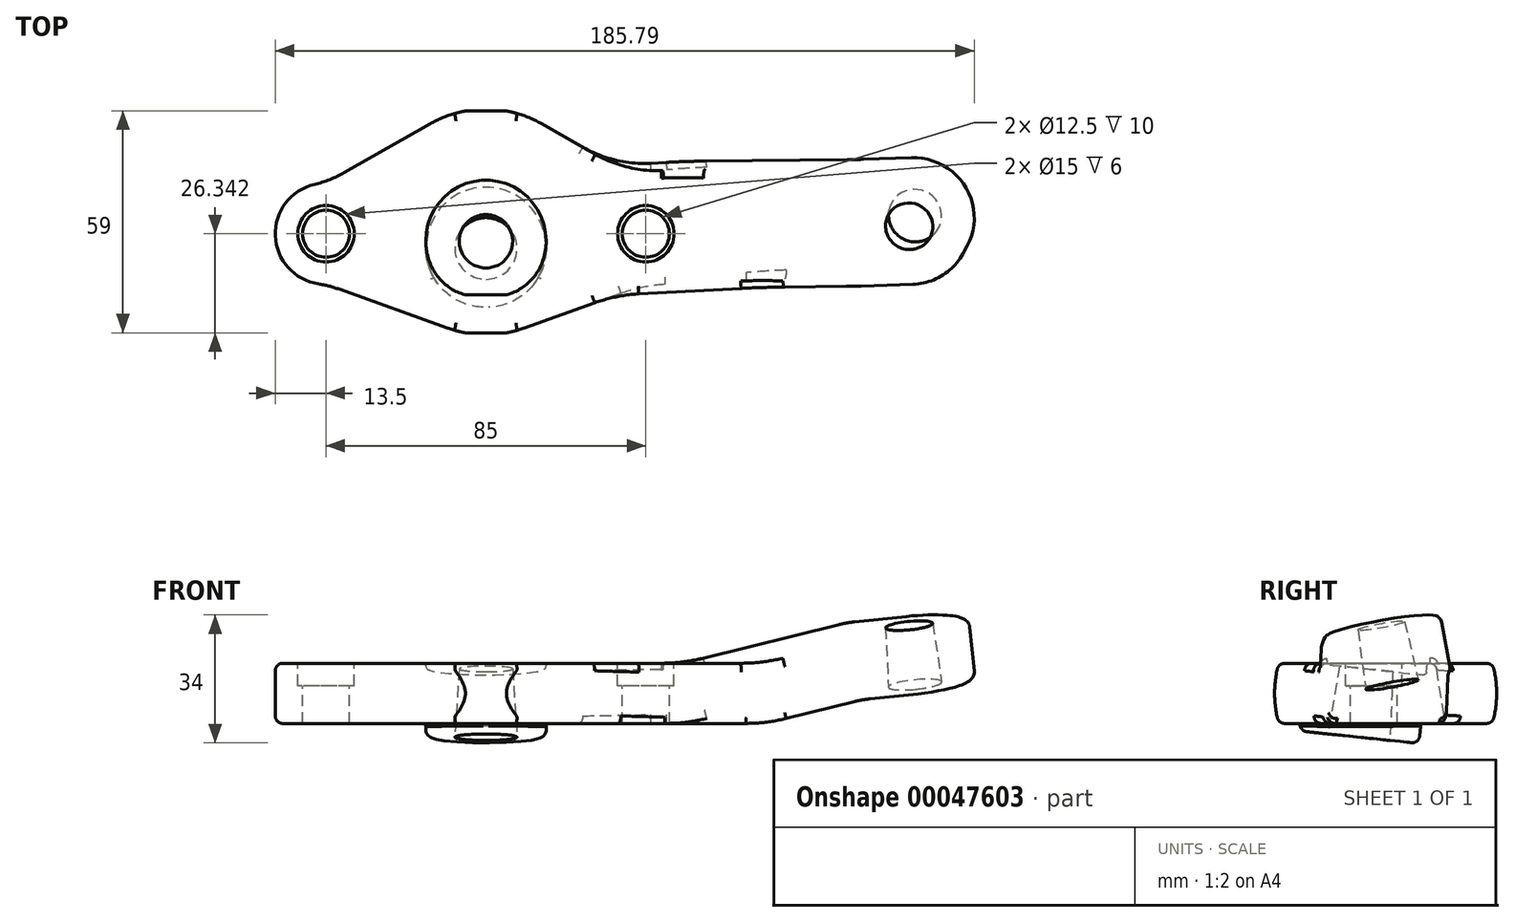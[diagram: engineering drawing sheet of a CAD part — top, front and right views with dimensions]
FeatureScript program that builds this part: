
annotation { "Feature Type Name" : "Feature", "Feature Type Description" : "" }
export const myFeature = defineFeature(function(context is Context, id is Id, definition is map)
    precondition{}
    {
        {
            var Q0;
            Q0=qCreatedBy(makeId("Top.planeOp"),FACE);
            var sketch = newSketch(context, id + "F0", { "sketchPlane" : qUnion([Q0])});
            skCircle(sketch, "E0", {"center": v(0, 0) * mm, "radius": 5 * mm});
            skCircle(sketch, "E1", {"center": v(0, 0) * mm, "radius": 15 * mm});
            skCircle(sketch, "E2", {"center": v(42.5, 1.84) * mm, "radius": 6.25 * mm});
            skCircle(sketch, "E3", {"center": v(42.5, 1.84) * mm, "radius": 7.5 * mm});
            skCircle(sketch, "E4", {"center": v(113.5, 5.65) * mm, "radius": 5 * mm});
            skArc(sketch, "E5", {"start": v(114.35, -10.32) * mm, "mid": v(129.47, 6.51) * mm, "end": v(112.63, 21.63) * mm});
            skCircle(sketch, "E6", {"center": v(-42.5, 1.84) * mm, "radius": 6.25 * mm});
            skCircle(sketch, "E7", {"center": v(-42.5, 1.84) * mm, "radius": 7.5 * mm});
            skLineSegment(sketch, "E8", {"start": v(-42.5, 25) * mm, "end": v(-42.5, -32.02) * mm, "construction": true});
            skArc(sketch, "E9", {"start": v(-44.55, -11.5) * mm, "mid": v(-55.99, 1.31) * mm, "end": v(-45.6, 14.98) * mm});
            skArc(sketch, "E10", {"start": v(-10.1, -23.25) * mm, "mid": v(0, -25) * mm, "end": v(10.1, -23.25) * mm});
            skLineSegment(sketch, "E11", {"start": v(-37.64, 18.1) * mm, "end": v(-14.83, 31.08) * mm});
            skLineSegment(sketch, "E12", {"start": v(-39.02, -12.9) * mm, "end": v(-10.1, -23.25) * mm});
            skLineSegment(sketch, "E13", {"start": v(42.5, 1.84) * mm, "end": v(113.5, 5.65) * mm, "construction": true});
            skLineSegment(sketch, "E14", {"start": v(112.63, 21.63) * mm, "end": v(47.23, 18.12) * mm});
            skLineSegment(sketch, "E15", {"start": v(114.35, -10.32) * mm, "end": v(38.57, -14.4) * mm});
            skLineSegment(sketch, "E16", {"start": v(42.5, -32.88) * mm, "end": v(42.5, 48.6) * mm, "construction": true});
            skArc(sketch, "E17", {"start": v(42.5, -11.66) * mm, "mid": v(56, 1.84) * mm, "end": v(42.5, 15.34) * mm, "construction": true});
            skLineSegment(sketch, "E18", {"start": v(30.8, 22) * mm, "end": v(14.83, 31.08) * mm});
            skLineSegment(sketch, "E19", {"start": v(30.08, -16.1) * mm, "end": v(10.1, -23.25) * mm});
            skArc(sketch, "E20.trimOffspring", {"start": v(14.83, 31.08) * mm, "mid": v(0, 35) * mm, "end": v(-14.83, 31.08) * mm});
            skArc(sketch, "E21.filletArc", {"start": v(30.8, 22) * mm, "mid": v(38.74, 18.88) * mm, "end": v(47.23, 18.12) * mm});
            skArc(sketch, "E22.filletArc", {"start": v(38.57, -14.4) * mm, "mid": v(34.26, -14.94) * mm, "end": v(30.08, -16.1) * mm});
            skPoint(sketch, "E23.visualSharp", {"position": v(-42.5, -11.66) * mm});
            skArc(sketch, "E23.filletArc", {"start": v(-39.02, -12.9) * mm, "mid": v(-41.75, -12.07) * mm, "end": v(-44.55, -11.5) * mm});
            skPoint(sketch, "E24.visualSharp", {"position": v(-42.5, 15.34) * mm});
            skArc(sketch, "E24.filletArc", {"start": v(-45.6, 14.98) * mm, "mid": v(-41.5, 16.26) * mm, "end": v(-37.64, 18.1) * mm});
            skLineSegment(sketch, "E25", {"start": v(96.66, 20.77) * mm, "end": v(98.37, -11.18) * mm});
            skSolve(sketch);
        }
        {
            var Q0;
            Q0=qCreatedBy(makeId("Top.planeOp"),FACE);
            cPlane(context, id + "F1", {"entities" : qUnion([Q0]), "cplaneType" : CPlaneType.OFFSET, "offset" : 10.43 * mm, "width" : 150 * mm, "height" : 150 * mm});
        }
        {
            var Q0;
            Q0=qCreatedBy(id+"F1.planeOp",FACE);
            var sketch = newSketch(context, id + "F2", { "sketchPlane" : qUnion([Q0])});
            skPoint(sketch, "E26.0", {"position": v(113.5, 5.65) * mm});
            skLineSegment(sketch, "E27", {"start": v(114.74, -17.54) * mm, "end": v(111.9, 35.31) * mm, "construction": true});
            skLineSegment(sketch, "E28.0", {"start": v(96.66, 20.77) * mm, "end": v(98.37, -11.18) * mm, "construction": true});
            skSolve(sketch);
        }
        {
            var Q0;
            Q0=sQuery(id+"F2.wireOp",EDGE,"E27");
            var Q1;
            Q1=qCreatedBy(id+"F1.planeOp",FACE);
            cPlane(context, id + "F3", {"entities" : qUnion([Q0, Q1]), "cplaneType" : CPlaneType.LINE_ANGLE, "offset" : 150 * mm, "angle" : 353.8 * degree, "width" : 150 * mm, "height" : 150 * mm});
        }
        {
            var Q0;
            Q0=qCreatedBy(id+"F3.planeOp",FACE);
            var sketch = newSketch(context, id + "F4", { "sketchPlane" : qUnion([Q0])});
            skLineSegment(sketch, "E29.0", {"start": v(42.25, -1.84) * mm, "end": v(112.83, -5.65) * mm});
            skSolve(sketch);
        }
        {
            var Q0;
            Q0=sQuery(id+"F4.wireOp",EDGE,"E29.0");
            var Q1;
            Q1=qCreatedBy(id+"F3.planeOp",FACE);
            cPlane(context, id + "F5", {"entities" : qUnion([Q0, Q1]), "cplaneType" : CPlaneType.LINE_ANGLE, "offset" : 150 * mm, "angle" : 9.9 * degree, "width" : 150 * mm, "height" : 150 * mm});
        }
        {
            var Q0;
            Q0=qCreatedBy(id+"F5.planeOp",FACE);
            var sketch = newSketch(context, id + "F6", { "sketchPlane" : qUnion([Q0])});
            skPoint(sketch, "E30.0", {"position": v(112.86, 5.56) * mm});
            skArc(sketch, "E31", {"start": v(113.7, -10.41) * mm, "mid": v(128.84, 6.41) * mm, "end": v(112, 21.54) * mm});
            skLineSegment(sketch, "E32.0", {"start": v(42.27, 1.81) * mm, "end": v(112.86, 5.56) * mm, "construction": true});
            skLineSegment(sketch, "E33", {"start": v(96.03, 20.7) * mm, "end": v(112, 21.54) * mm});
            skLineSegment(sketch, "E34", {"start": v(97.73, -11.26) * mm, "end": v(113.7, -10.41) * mm});
            skLineSegment(sketch, "E35", {"start": v(96.03, 20.7) * mm, "end": v(97.73, -11.26) * mm});
            skCircle(sketch, "E36", {"center": v(112.86, 5.56) * mm, "radius": 5 * mm});
            skSolve(sketch);
        }
        {
            var Q0;
            Q0=makeQuery(id+"F6.imprint","IMPRINT",FACE,{"disambiguationData":[TD([[makeQuery(id+"F6.imprint","IMPRINT",EDGE,{"derivedFrom":sQuery(id+"F6.wireOp",EDGE,"E31")}),1.0]])]});
            extrude(context, id + "F7", {"entities" : qUnion([Q0]), "oppositeDirection" : true, "depth" : 16 * mm});
        }
        {
            var Q0;
            Q0=sQuery(id+"F6.wireOp",EDGE,"E35");
            var Q1;
            Q1=qCreatedBy(id+"F5.planeOp",FACE);
            cPlane(context, id + "F8", {"entities" : qUnion([Q0, Q1]), "cplaneType" : CPlaneType.LINE_ANGLE, "offset" : 150 * mm, "angle" : 8 * degree, "width" : 150 * mm, "height" : 150 * mm});
        }
        {
            var Q0;
            Q0=qCreatedBy(id+"F8.planeOp",FACE);
            var sketch = newSketch(context, id + "F9", { "sketchPlane" : qUnion([Q0])});
            skLineSegment(sketch, "E37.0", {"start": v(94.81, -20.75) * mm, "end": v(96.55, 11.2) * mm});
            skLineSegment(sketch, "E38.0", {"start": v(41.6, -1.83) * mm, "end": v(111.5, -5.63) * mm, "construction": true});
            skLineSegment(sketch, "E39", {"start": v(94.81, -20.75) * mm, "end": v(24.92, -16.95) * mm});
            skLineSegment(sketch, "E40", {"start": v(96.55, 11.2) * mm, "end": v(26.65, 15) * mm});
            skLineSegment(sketch, "E41", {"start": v(24.92, -16.95) * mm, "end": v(26.65, 15) * mm});
            skSolve(sketch);
        }
        {
            var Q0;
            Q0 = qSketchRegion(id + "F9", true);
            extrude(context, id + "F10", {"entities" : qUnion([Q0]), "operationType" : NewBodyOperationType.ADD, "depth" : 16 * mm});
        }
        {
            var Q0;
            Q0=qCreatedBy(makeId("Top.planeOp"),FACE);
            var sketch = newSketch(context, id + "F11", { "sketchPlane" : qUnion([Q0])});
            skLineSegment(sketch, "E42.0", {"start": v(30.8, 22) * mm, "end": v(14.83, 31.08) * mm});
            skArc(sketch, "E43.0", {"start": v(14.83, 31.08) * mm, "mid": v(0, 35) * mm, "end": v(-14.83, 31.08) * mm});
            skLineSegment(sketch, "E44.0", {"start": v(-37.64, 18.1) * mm, "end": v(-14.83, 31.08) * mm});
            skArc(sketch, "E45.0", {"start": v(-45.6, 14.98) * mm, "mid": v(-41.5, 16.26) * mm, "end": v(-37.64, 18.1) * mm});
            skArc(sketch, "E46.0", {"start": v(-44.55, -11.5) * mm, "mid": v(-55.99, 1.31) * mm, "end": v(-45.6, 14.98) * mm});
            skArc(sketch, "E47.0", {"start": v(-39.02, -12.9) * mm, "mid": v(-41.75, -12.07) * mm, "end": v(-44.55, -11.5) * mm});
            skLineSegment(sketch, "E48.0", {"start": v(-39.02, -12.9) * mm, "end": v(-10.1, -23.25) * mm});
            skArc(sketch, "E49.0", {"start": v(-10.1, -23.25) * mm, "mid": v(0, -25) * mm, "end": v(10.1, -23.25) * mm});
            skLineSegment(sketch, "E50.0", {"start": v(30.08, -16.1) * mm, "end": v(10.1, -23.25) * mm});
            skCircle(sketch, "E51.0", {"center": v(0, 0) * mm, "radius": 5 * mm});
            skCircle(sketch, "E52.0", {"center": v(-42.5, 1.84) * mm, "radius": 6.25 * mm});
            skCircle(sketch, "E53.0", {"center": v(42.5, 1.84) * mm, "radius": 6.25 * mm});
            skLineSegment(sketch, "E54.0", {"start": v(95.75, 19.02) * mm, "end": v(37.09, 18.42) * mm});
            skLineSegment(sketch, "E55.0", {"start": v(97.44, -12.45) * mm, "end": v(38.6, -13.05) * mm});
            skLineSegment(sketch, "E56", {"start": v(30.8, 22) * mm, "end": v(37.09, 18.42) * mm});
            skLineSegment(sketch, "E57", {"start": v(30.08, -16.1) * mm, "end": v(38.6, -13.05) * mm});
            skPoint(sketch, "E58.orphan", {"position": v(27.8, 18.33) * mm});
            skPoint(sketch, "E59.orphan", {"position": v(29.5, -13.15) * mm});
            skLineSegment(sketch, "E60", {"start": v(59.21, 18.65) * mm, "end": v(83.19, -12.6) * mm});
            skSolve(sketch);
        }
        {
            var Q0;
            Q0=makeQuery(id+"F11.imprint","IMPRINT",FACE,{"disambiguationData":[TD([[makeQuery(id+"F11.imprint","IMPRINT",EDGE,{"derivedFrom":sQuery(id+"F11.wireOp",EDGE,"E42.0")}),1.0]])]});
            var Q1;
            Q1=makeQuery(id+"F11.imprint","IMPRINT",FACE,{"disambiguationData":[TD([[makeQuery(id+"F11.imprint","IMPRINT",EDGE,{"derivedFrom":sQuery(id+"F11.wireOp",EDGE,"E51.0")}),1.0]])]});
            extrude(context, id + "F12", {"entities" : qUnion([Q0, Q1]), "oppositeDirection" : true, "depth" : 16 * mm});
        }
        {
            var Q0;
            Q0=makeQuery(id+"F10.opExtrude","CAP_FACE",FACE,{"disambiguationData":[OSD([sQuery(id+"F9.wireOp",EDGE,"E37.0"),sQuery(id+"F9.wireOp",EDGE,"E39"),sQuery(id+"F9.wireOp",EDGE,"E40"),sQuery(id+"F9.wireOp",EDGE,"E41")])],"isStart":false});
            var sketch = newSketch(context, id + "F13", { "sketchPlane" : qUnion([Q0])});
            skLineSegment(sketch, "E61.bottom", {"start": v(81.18, -25.69) * mm, "end": v(41.74, -25.69) * mm});
            skLineSegment(sketch, "E61.top", {"start": v(81.18, 28.04) * mm, "end": v(41.74, 28.04) * mm});
            skLineSegment(sketch, "E61.left", {"start": v(81.18, -25.69) * mm, "end": v(81.18, 28.04) * mm});
            skLineSegment(sketch, "E61.right", {"start": v(41.74, -25.69) * mm, "end": v(41.74, 28.04) * mm});
            skSolve(sketch);
        }
        {
            var Q0;
            Q0 = qSketchRegion(id + "F13", true);
            extrude(context, id + "F14", {"entities" : qUnion([Q0]), "operationType" : NewBodyOperationType.REMOVE, "endBound" : BoundingType.THROUGH_ALL, "depth" : 25 * mm});
        }
        {
            var Q0;
            Q0=makeQuery(id+"F12.opExtrude","CAP_FACE",FACE,{"disambiguationData":[OSD([sQuery(id+"F11.wireOp",EDGE,"E42.0"),sQuery(id+"F11.wireOp",EDGE,"E43.0"),sQuery(id+"F11.wireOp",EDGE,"E44.0"),sQuery(id+"F11.wireOp",EDGE,"E45.0"),sQuery(id+"F11.wireOp",EDGE,"E46.0"),sQuery(id+"F11.wireOp",EDGE,"E47.0"),sQuery(id+"F11.wireOp",EDGE,"E48.0"),sQuery(id+"F11.wireOp",EDGE,"E49.0"),sQuery(id+"F11.wireOp",EDGE,"E50.0"),sQuery(id+"F11.wireOp",EDGE,"E51.0"),sQuery(id+"F11.wireOp",EDGE,"E52.0"),sQuery(id+"F11.wireOp",EDGE,"E53.0"),sQuery(id+"F11.wireOp",EDGE,"E54.0"),sQuery(id+"F11.wireOp",EDGE,"E55.0"),sQuery(id+"F11.wireOp",EDGE,"E56"),sQuery(id+"F11.wireOp",EDGE,"E57"),sQuery(id+"F11.wireOp",EDGE,"E60")])],"isStart":false});
            var sketch = newSketch(context, id + "F15", { "sketchPlane" : qUnion([Q0])});
            skLineSegment(sketch, "E62.bottom", {"start": v(87.5, -32.8) * mm, "end": v(14.56, -32.8) * mm});
            skLineSegment(sketch, "E62.top", {"start": v(87.5, 19.74) * mm, "end": v(14.56, 19.74) * mm});
            skLineSegment(sketch, "E62.left", {"start": v(87.5, -32.8) * mm, "end": v(87.5, 19.74) * mm});
            skLineSegment(sketch, "E62.right", {"start": v(14.56, -32.8) * mm, "end": v(14.56, 19.74) * mm});
            skSolve(sketch);
        }
        {
            var Q0;
            Q0 = qSketchRegion(id + "F15", true);
            extrude(context, id + "F16", {"entities" : qUnion([Q0]), "operationType" : NewBodyOperationType.REMOVE, "endBound" : BoundingType.THROUGH_ALL, "depth" : 25 * mm});
        }
        {
            var Q0;
            Q0=makeQuery(id+"F7.opExtrude","SWEPT_BODY",BODY,{"disambiguationData":[OSD([sQuery(id+"F6.wireOp",EDGE,"E31"),sQuery(id+"F6.wireOp",EDGE,"E33"),sQuery(id+"F6.wireOp",EDGE,"E34"),sQuery(id+"F6.wireOp",EDGE,"E35"),sQuery(id+"F6.wireOp",EDGE,"E36")])]});
            var Q1;
            Q1=makeQuery(id+"F12.opExtrude","SWEPT_BODY",BODY,{"disambiguationData":[OSD([sQuery(id+"F11.wireOp",EDGE,"E42.0"),sQuery(id+"F11.wireOp",EDGE,"E43.0"),sQuery(id+"F11.wireOp",EDGE,"E44.0"),sQuery(id+"F11.wireOp",EDGE,"E45.0"),sQuery(id+"F11.wireOp",EDGE,"E46.0"),sQuery(id+"F11.wireOp",EDGE,"E47.0"),sQuery(id+"F11.wireOp",EDGE,"E48.0"),sQuery(id+"F11.wireOp",EDGE,"E49.0"),sQuery(id+"F11.wireOp",EDGE,"E50.0"),sQuery(id+"F11.wireOp",EDGE,"E51.0"),sQuery(id+"F11.wireOp",EDGE,"E52.0"),sQuery(id+"F11.wireOp",EDGE,"E53.0"),sQuery(id+"F11.wireOp",EDGE,"E54.0"),sQuery(id+"F11.wireOp",EDGE,"E55.0"),sQuery(id+"F11.wireOp",EDGE,"E56"),sQuery(id+"F11.wireOp",EDGE,"E57"),sQuery(id+"F11.wireOp",EDGE,"E60")])]});
            booleanBodies(context, id + "F17", {"operationType" : BooleanOperationType.UNION, "tools" : qUnion([Q0, Q1])});
        }
        {
            var Q0;
            Q0=makeQuery(id+"F10.boolean.opBoolean","MERGE",FACE,{"derivedFrom":[makeQuery(id+"F7.opExtrude","SWEPT_FACE",FACE,{"disambiguationData":[OSD([sQuery(id+"F6.wireOp",EDGE,"E34")])]}),makeQuery(id+"F10.opExtrude","SWEPT_FACE",FACE,{"disambiguationData":[OSD([sQuery(id+"F9.wireOp",EDGE,"E40")])]})]});
            var sketch = newSketch(context, id + "F18", { "sketchPlane" : qUnion([Q0])});
            skLineSegment(sketch, "E63.0", {"start": v(96.71, 7.63) * mm, "end": v(74.21, 2.2) * mm});
            skLineSegment(sketch, "E64.0", {"start": v(37.72, -13.5) * mm, "end": v(37.86, 2.26) * mm});
            skLineSegment(sketch, "E65", {"start": v(74.21, 2.2) * mm, "end": v(37.78, -6.6) * mm});
            skLineSegment(sketch, "E66", {"start": v(37.78, -6.6) * mm, "end": v(37.78, -26.46) * mm});
            skLineSegment(sketch, "E67", {"start": v(37.78, -26.46) * mm, "end": v(90.45, -23.8) * mm});
            skLineSegment(sketch, "E68", {"start": v(90.45, -23.8) * mm, "end": v(96.71, 7.63) * mm});
            skSolve(sketch);
        }
        {
            var Q0;
            Q0 = qSketchRegion(id + "F18", true);
            extrude(context, id + "F19", {"entities" : qUnion([Q0]), "operationType" : NewBodyOperationType.REMOVE, "endBound" : BoundingType.THROUGH_ALL, "depth" : 25 * mm});
        }
        {
            var Q0;
            Q0=makeQuery(id+"F10.boolean.opBoolean","MERGE",FACE,{"derivedFrom":[makeQuery(id+"F7.opExtrude","SWEPT_FACE",FACE,{"disambiguationData":[OSD([sQuery(id+"F6.wireOp",EDGE,"E33")])]}),makeQuery(id+"F10.opExtrude","SWEPT_FACE",FACE,{"disambiguationData":[OSD([sQuery(id+"F9.wireOp",EDGE,"E39")])]})]});
            var sketch = newSketch(context, id + "F20", { "sketchPlane" : qUnion([Q0])});
            skLineSegment(sketch, "E69.0", {"start": v(-37.96, -6.56) * mm, "end": v(-34.4, -19.3) * mm});
            skLineSegment(sketch, "E70", {"start": v(-37.96, -6.56) * mm, "end": v(-41.47, 6) * mm});
            skLineSegment(sketch, "E71", {"start": v(-41.47, 6) * mm, "end": v(-64.2, -1.75) * mm});
            skLineSegment(sketch, "E72", {"start": v(-64.2, -1.75) * mm, "end": v(-47.46, -32.44) * mm});
            skLineSegment(sketch, "E73", {"start": v(-47.46, -32.44) * mm, "end": v(-34.4, -19.3) * mm});
            skSolve(sketch);
        }
        {
            var Q0;
            Q0 = qSketchRegion(id + "F20", true);
            extrude(context, id + "F21", {"entities" : qUnion([Q0]), "operationType" : NewBodyOperationType.REMOVE, "endBound" : BoundingType.THROUGH_ALL, "depth" : 25 * mm});
        }
        {
            var Q0;
            Q0=makeQuery(id+"F12.opExtrude","SWEPT_FACE",FACE,{"disambiguationData":[OSD([sQuery(id+"F11.wireOp",EDGE,"E42.0"),sQuery(id+"F11.wireOp",EDGE,"E56")])]});
            var sketch = newSketch(context, id + "F22", { "sketchPlane" : qUnion([Q0])});
            skLineSegment(sketch, "E74.0", {"start": v(-23.13, -3.42) * mm, "end": v(-19.04, -16) * mm});
            skLineSegment(sketch, "E75", {"start": v(-23.13, -3.42) * mm, "end": v(-25.87, 5.02) * mm});
            skLineSegment(sketch, "E76", {"start": v(-25.87, 5.02) * mm, "end": v(-20.04, 3.08) * mm});
            skLineSegment(sketch, "E77", {"start": v(-20.04, 3.08) * mm, "end": v(-21.79, -7.55) * mm});
            skSolve(sketch);
        }
        {
            var Q0;
            Q0 = qSketchRegion(id + "F22", true);
            extrude(context, id + "F23", {"entities" : qUnion([Q0]), "operationType" : NewBodyOperationType.REMOVE, "depth" : 25 * mm});
        }
        {
            var Q0;
            Q0=makeQuery(id+"F12.opExtrude","SWEPT_FACE",FACE,{"disambiguationData":[OSD([sQuery(id+"F11.wireOp",EDGE,"E50.0"),sQuery(id+"F11.wireOp",EDGE,"E57")])]});
            var sketch = newSketch(context, id + "F24", { "sketchPlane" : qUnion([Q0])});
            skLineSegment(sketch, "E78.0.0", {"start": v(31.95, 0) * mm, "end": v(1.68, 0) * mm});
            skLineSegment(sketch, "E78.0.1", {"start": v(1.68, 0) * mm, "end": v(1.68, -16) * mm});
            skLineSegment(sketch, "E78.0.2", {"start": v(1.68, -16) * mm, "end": v(31.95, -16) * mm});
            skLineSegment(sketch, "E79", {"start": v(31.95, -16) * mm, "end": v(55.92, -16) * mm});
            skLineSegment(sketch, "E80", {"start": v(55.92, -16) * mm, "end": v(55.92, 0) * mm});
            skLineSegment(sketch, "E81", {"start": v(55.92, 0) * mm, "end": v(31.95, 0) * mm});
            skSolve(sketch);
        }
        {
            var Q0;
            Q0 = qSketchRegion(id + "F24", true);
            extrude(context, id + "F25", {"entities" : qUnion([Q0]), "operationType" : NewBodyOperationType.ADD, "oppositeDirection" : true, "depth" : 5 * mm});
        }
        {
            var Q0;
            Q0=makeQuery(id+"F19.boolean.opBoolean","MERGE",FACE,{"derivedFrom":[makeQuery(id+"F10.boolean.opBoolean","MERGE",FACE,{"derivedFrom":[makeQuery(id+"F7.opExtrude","SWEPT_FACE",FACE,{"disambiguationData":[OSD([sQuery(id+"F6.wireOp",EDGE,"E34")])]}),makeQuery(id+"F10.opExtrude","SWEPT_FACE",FACE,{"disambiguationData":[OSD([sQuery(id+"F9.wireOp",EDGE,"E40")])]})]}),makeQuery(id+"F19.opExtrude","CAP_FACE",FACE,{"disambiguationData":[OSD([sQuery(id+"F18.wireOp",EDGE,"E63.0"),sQuery(id+"F18.wireOp",EDGE,"E65"),sQuery(id+"F18.wireOp",EDGE,"E66"),sQuery(id+"F18.wireOp",EDGE,"E67"),sQuery(id+"F18.wireOp",EDGE,"E68")])],"isStart":true})]});
            var sketch = newSketch(context, id + "F26", { "sketchPlane" : qUnion([Q0])});
            skLineSegment(sketch, "E82.0", {"start": v(41.84, -13.75) * mm, "end": v(37.78, -6.6) * mm});
            skLineSegment(sketch, "E83.0", {"start": v(75.07, -14.06) * mm, "end": v(41.84, -13.75) * mm});
            skLineSegment(sketch, "E84", {"start": v(37.78, -6.6) * mm, "end": v(31.92, 3.74) * mm});
            skPoint(sketch, "E85.0", {"position": v(74.21, 2.2) * mm});
            skLineSegment(sketch, "E86", {"start": v(31.92, 3.74) * mm, "end": v(74.21, 2.2) * mm});
            skLineSegment(sketch, "E87", {"start": v(74.21, 2.2) * mm, "end": v(75.07, -14.06) * mm});
            skSolve(sketch);
        }
        {
            var Q0;
            Q0 = qSketchRegion(id + "F26", true);
            extrude(context, id + "F27", {"entities" : qUnion([Q0]), "operationType" : NewBodyOperationType.ADD, "oppositeDirection" : true, "depth" : 5 * mm});
        }
        {
            var Q0;
            {var subQ0=sQuery(id+"F11.wireOp",EDGE,"E45.0");var subQ2=sQuery(id+"F11.wireOp",EDGE,"E44.0");var subQ3=sQuery(id+"F11.wireOp",EDGE,"E43.0");var subQ4=sQuery(id+"F11.wireOp",EDGE,"E56");var subQ5=sQuery(id+"F11.wireOp",EDGE,"E42.0");var subQ6=sQuery(id+"F11.wireOp",EDGE,"E57");var subQ7=sQuery(id+"F11.wireOp",EDGE,"E55.0");var subQ8=sQuery(id+"F11.wireOp",EDGE,"E54.0");var subQ9=sQuery(id+"F11.wireOp",EDGE,"E53.0");var subQ10=sQuery(id+"F11.wireOp",EDGE,"E52.0");var subQ11=sQuery(id+"F11.wireOp",EDGE,"E51.0");var subQ12=sQuery(id+"F11.wireOp",EDGE,"E50.0");var subQ13=sQuery(id+"F11.wireOp",EDGE,"E49.0");var subQ14=sQuery(id+"F11.wireOp",EDGE,"E48.0");var subQ15=sQuery(id+"F11.wireOp",EDGE,"E47.0");var subQ16=sQuery(id+"F11.wireOp",EDGE,"E46.0");var subQ17=makeQuery(id+"F12.opExtrude","CAP_FACE",FACE,{"disambiguationData":[OSD([subQ5,subQ3,subQ2,subQ0,subQ16,subQ15,subQ14,subQ13,subQ12,subQ11,subQ10,subQ9,subQ8,subQ7,subQ4,subQ6,sQuery(id+"F11.wireOp",EDGE,"E60")])],"isStart":true});Q0=makeQuery(id+"F17.opBoolean","SPLIT",FACE,{"disambiguationData":[TD([makeQuery(id+"F7.opExtrude","SWEPT_FACE",FACE,{"disambiguationData":[OSD([sQuery(id+"F6.wireOp",EDGE,"E33")])]})])],"derivedFrom":subQ17});}
            var sketch = newSketch(context, id + "F28", { "sketchPlane" : qUnion([Q0])});
            skLineSegment(sketch, "E88.0", {"start": v(50.91, 18.56) * mm, "end": v(71.22, -7.8) * mm});
            skLineSegment(sketch, "E89", {"start": v(71.22, -7.8) * mm, "end": v(80.14, -19.39) * mm});
            skLineSegment(sketch, "E90", {"start": v(80.14, -19.39) * mm, "end": v(31.07, -19.75) * mm});
            skLineSegment(sketch, "E91", {"start": v(31.07, -19.75) * mm, "end": v(28.54, -5.23) * mm});
            skLineSegment(sketch, "E92", {"start": v(28.54, -5.23) * mm, "end": v(50.91, 18.56) * mm});
            skSolve(sketch);
        }
        {
            var Q0;
            Q0 = qSketchRegion(id + "F28", true);
            extrude(context, id + "F29", {"entities" : qUnion([Q0]), "operationType" : NewBodyOperationType.REMOVE, "endBound" : BoundingType.THROUGH_ALL, "depth" : 25 * mm});
        }
        {
            var Q0;
            {var subQ0=sQuery(id+"F9.wireOp",EDGE,"E39");var subQ1=sQuery(id+"F6.wireOp",EDGE,"E33");var subQ2=sQuery(id+"F9.wireOp",EDGE,"E40");Q0=makeQuery(id+"F17.opBoolean","SPLIT",FACE,{"disambiguationData":[TD([makeQuery(id+"F7.opExtrude","SWEPT_FACE",FACE,{"disambiguationData":[OSD([subQ1])]})])],"derivedFrom":makeQuery(id+"F10.opExtrude","CAP_FACE",FACE,{"disambiguationData":[OSD([sQuery(id+"F9.wireOp",EDGE,"E37.0"),subQ0,subQ2,sQuery(id+"F9.wireOp",EDGE,"E41")])],"isStart":true})});}
            var sketch = newSketch(context, id + "F30", { "sketchPlane" : qUnion([Q0])});
            skLineSegment(sketch, "E93.0", {"start": v(48.69, 18.24) * mm, "end": v(69.57, -7.66) * mm});
            skLineSegment(sketch, "E94", {"start": v(69.57, -7.66) * mm, "end": v(77.97, -18.09) * mm});
            skLineSegment(sketch, "E95", {"start": v(77.97, -18.09) * mm, "end": v(80.73, -17.42) * mm});
            skLineSegment(sketch, "E96", {"start": v(80.73, -17.42) * mm, "end": v(68.77, 15.52) * mm});
            skLineSegment(sketch, "E97", {"start": v(68.77, 15.52) * mm, "end": v(48.69, 18.24) * mm});
            skSolve(sketch);
        }
        {
            var Q0;
            Q0 = qSketchRegion(id + "F30", true);
            extrude(context, id + "F31", {"entities" : qUnion([Q0]), "operationType" : NewBodyOperationType.REMOVE, "endBound" : BoundingType.THROUGH_ALL, "depth" : 25 * mm});
        }
        {
            var Q0;
            Q0=makeQuery(id+"F12.opExtrude","SWEPT_FACE",FACE,{"disambiguationData":[OSD([sQuery(id+"F11.wireOp",EDGE,"E50.0"),sQuery(id+"F11.wireOp",EDGE,"E57")])]});
            var sketch = newSketch(context, id + "F32", { "sketchPlane" : qUnion([Q0])});
            skLineSegment(sketch, "E98.0", {"start": v(36.25, -16) * mm, "end": v(31.95, -9) * mm});
            skLineSegment(sketch, "E99.0", {"start": v(31.95, -9) * mm, "end": v(26.42, 0) * mm});
            skLineSegment(sketch, "E100", {"start": v(26.42, 0) * mm, "end": v(26.42, -16) * mm});
            skLineSegment(sketch, "E101", {"start": v(26.42, -16) * mm, "end": v(36.25, -16) * mm});
            skSolve(sketch);
        }
        {
            var Q0;
            Q0 = qSketchRegion(id + "F32", true);
            extrude(context, id + "F33", {"entities" : qUnion([Q0]), "operationType" : NewBodyOperationType.REMOVE, "endBound" : BoundingType.THROUGH_ALL, "depth" : 25 * mm});
        }
        {
            var Q0;
            Q0=makeQuery(id+"F11.imprint","IMPRINT",FACE,{"disambiguationData":[TD([[makeQuery(id+"F11.imprint","IMPRINT",EDGE,{"derivedFrom":sQuery(id+"F11.wireOp",EDGE,"E53.0")}),1.0]])]});
            extrude(context, id + "F34", {"entities" : qUnion([Q0]), "operationType" : NewBodyOperationType.REMOVE, "endBound" : BoundingType.THROUGH_ALL, "oppositeDirection" : true, "depth" : 25 * mm});
        }
        {
            var Q0;
            Q0=makeQuery(id+"F23.boolean.opBoolean","MERGE",EDGE,{"derivedFrom":[makeQuery(id+"F17.opBoolean","INTERSECT",EDGE,{"derivedFrom":[makeQuery(id+"F12.opExtrude","SWEPT_FACE",FACE,{"disambiguationData":[OSD([sQuery(id+"F11.wireOp",EDGE,"E42.0"),sQuery(id+"F11.wireOp",EDGE,"E56")])]}),makeQuery(id+"F10.boolean.opBoolean","MERGE",FACE,{"derivedFrom":[makeQuery(id+"F7.opExtrude","SWEPT_FACE",FACE,{"disambiguationData":[OSD([sQuery(id+"F6.wireOp",EDGE,"E33")])]}),makeQuery(id+"F10.opExtrude","SWEPT_FACE",FACE,{"disambiguationData":[OSD([sQuery(id+"F9.wireOp",EDGE,"E39")])]})]})]}),makeQuery(id+"F21.boolean.opBoolean","COPY",EDGE,{"derivedFrom":makeQuery(id+"F21.opExtrude","CAP_EDGE",EDGE,{"disambiguationData":[OSD([sQuery(id+"F20.wireOp",EDGE,"E69.0"),sQuery(id+"F20.wireOp",EDGE,"E70")])],"isStart":true})}),makeQuery(id+"F23.opExtrude","CAP_EDGE",EDGE,{"disambiguationData":[OSD([sQuery(id+"F22.wireOp",EDGE,"E74.0"),sQuery(id+"F22.wireOp",EDGE,"E75")])],"isStart":true})]});
            var Q1;
            {var subQ2=makeQuery(id+"F7.opExtrude","SWEPT_FACE",FACE,{"disambiguationData":[OSD([sQuery(id+"F6.wireOp",EDGE,"E34")])]});var subQ3=sQuery(id+"F26.wireOp",EDGE,"E84");var subQ4=sQuery(id+"F26.wireOp",EDGE,"E82.0");var subQ5=sQuery(id+"F11.wireOp",EDGE,"E55.0");var subQ6=makeQuery(id+"F10.opExtrude","SWEPT_FACE",FACE,{"disambiguationData":[OSD([sQuery(id+"F9.wireOp",EDGE,"E40")])]});var subQ7=sQuery(id+"F18.wireOp",EDGE,"E66");var subQ8=makeQuery(id+"F19.opExtrude","CAP_FACE",FACE,{"disambiguationData":[OSD([sQuery(id+"F18.wireOp",EDGE,"E63.0"),sQuery(id+"F18.wireOp",EDGE,"E65"),subQ7,sQuery(id+"F18.wireOp",EDGE,"E67"),sQuery(id+"F18.wireOp",EDGE,"E68")])],"isStart":true});var subQ9=makeQuery(id+"F25.opExtrude","CAP_FACE",FACE,{"disambiguationData":[OSD([sQuery(id+"F24.wireOp",EDGE,"E78.0.0"),sQuery(id+"F24.wireOp",EDGE,"E78.0.1"),sQuery(id+"F24.wireOp",EDGE,"E78.0.2"),sQuery(id+"F24.wireOp",EDGE,"E79"),sQuery(id+"F24.wireOp",EDGE,"E80"),sQuery(id+"F24.wireOp",EDGE,"E81")])],"isStart":true});Q1=makeQuery(id+"F33.boolean.opBoolean","MERGE",EDGE,{"derivedFrom":[makeQuery(id+"F25.boolean.opBoolean","INTERSECT",EDGE,{"derivedFrom":[makeQuery(id+"F19.boolean.opBoolean","MERGE",FACE,{"derivedFrom":[makeQuery(id+"F10.boolean.opBoolean","MERGE",FACE,{"derivedFrom":[subQ2,subQ6]}),subQ8]}),subQ9]}),makeQuery(id+"F27.boolean.opBoolean","SPLIT",EDGE,{"disambiguationData":[TD([makeQuery(id+"F12.opExtrude","SWEPT_FACE",FACE,{"disambiguationData":[OSD([subQ5])]})])],"derivedFrom":makeQuery(id+"F27.opExtrude","CAP_EDGE",EDGE,{"disambiguationData":[OSD([subQ4,subQ3])],"isStart":true})})]});}
            fillet(context, id + "F35", {"entities" : qUnion([Q0, Q1]), "radius" : 30 * mm, "tangentPropagation" : true, "allowEdgeOverflow" : false});
        }
        {
            var Q0;
            {var subQ0=sQuery(id+"F11.wireOp",EDGE,"E45.0");var subQ2=sQuery(id+"F11.wireOp",EDGE,"E44.0");var subQ3=sQuery(id+"F11.wireOp",EDGE,"E43.0");var subQ4=sQuery(id+"F11.wireOp",EDGE,"E56");var subQ5=sQuery(id+"F11.wireOp",EDGE,"E42.0");var subQ6=sQuery(id+"F11.wireOp",EDGE,"E57");var subQ7=sQuery(id+"F11.wireOp",EDGE,"E55.0");var subQ8=sQuery(id+"F11.wireOp",EDGE,"E54.0");var subQ9=sQuery(id+"F11.wireOp",EDGE,"E53.0");var subQ10=sQuery(id+"F11.wireOp",EDGE,"E52.0");var subQ11=sQuery(id+"F11.wireOp",EDGE,"E51.0");var subQ12=sQuery(id+"F11.wireOp",EDGE,"E50.0");var subQ13=sQuery(id+"F11.wireOp",EDGE,"E49.0");var subQ14=sQuery(id+"F11.wireOp",EDGE,"E48.0");var subQ15=sQuery(id+"F11.wireOp",EDGE,"E47.0");var subQ16=sQuery(id+"F11.wireOp",EDGE,"E46.0");var subQ17=makeQuery(id+"F12.opExtrude","CAP_FACE",FACE,{"disambiguationData":[OSD([subQ5,subQ3,subQ2,subQ0,subQ16,subQ15,subQ14,subQ13,subQ12,subQ11,subQ10,subQ9,subQ8,subQ7,subQ4,subQ6,sQuery(id+"F11.wireOp",EDGE,"E60")])],"isStart":true});Q0=makeQuery(id+"F29.boolean.opBoolean","MERGE",FACE,{"derivedFrom":[makeQuery(id+"F17.opBoolean","SPLIT",FACE,{"disambiguationData":[TD([makeQuery(id+"F7.opExtrude","SWEPT_FACE",FACE,{"disambiguationData":[OSD([sQuery(id+"F6.wireOp",EDGE,"E33")])]})])],"derivedFrom":subQ17}),makeQuery(id+"F29.opExtrude","CAP_FACE",FACE,{"disambiguationData":[OSD([sQuery(id+"F28.wireOp",EDGE,"E88.0"),sQuery(id+"F28.wireOp",EDGE,"E89"),sQuery(id+"F28.wireOp",EDGE,"E90"),sQuery(id+"F28.wireOp",EDGE,"E91"),sQuery(id+"F28.wireOp",EDGE,"E92")])],"isStart":true})]});}
            var sketch = newSketch(context, id + "F36", { "sketchPlane" : qUnion([Q0])});
            skLineSegment(sketch, "E102", {"start": v(-42.5, 1.84) * mm, "end": v(42.5, 1.84) * mm, "construction": true});
            skLineSegment(sketch, "E103", {"start": v(-34.92, 0) * mm, "end": v(32.46, 0) * mm, "construction": true});
            skSolve(sketch);
        }
        {
            var Q0;
            Q0=sQuery(id+"F36.wireOp",EDGE,"E103");
            var Q1;
            Q1=makeQuery(id+"F11.imprint","IMPRINT",FACE,{"disambiguationData":[TD([[makeQuery(id+"F11.imprint","IMPRINT",EDGE,{"derivedFrom":sQuery(id+"F11.wireOp",EDGE,"E42.0")}),1.0]])]});
            cPlane(context, id + "F37", {"entities" : qUnion([Q0, Q1]), "cplaneType" : CPlaneType.LINE_ANGLE, "offset" : 150 * mm, "angle" : 354 * degree, "width" : 150 * mm, "height" : 150 * mm});
        }
        {
            var Q0;
            Q0=qCreatedBy(id+"F37.planeOp",FACE);
            var sketch = newSketch(context, id + "F38", { "sketchPlane" : qUnion([Q0])});
            skPoint(sketch, "E104.0", {"position": v(0, 0) * mm});
            skCircle(sketch, "E105", {"center": v(0, 0) * mm, "radius": 16 * mm});
            skSolve(sketch);
        }
        {
            var Q0;
            Q0 = qSketchRegion(id + "F38", true);
            extrude(context, id + "F39", {"entities" : qUnion([Q0]), "operationType" : NewBodyOperationType.REMOVE, "depth" : 1.5 * mm, "hasSecondDirection" : true, "secondDirectionBound" : BoundingType.THROUGH_ALL, "secondDirectionOppositeDirection" : true, "secondDirectionDepth" : 25 * mm});
        }
        {
            var Q0;
            Q0=makeQuery(id+"F39.boolean.opBoolean","COPY",FACE,{"derivedFrom":makeQuery(id+"F39.opExtrude","CAP_FACE",FACE,{"disambiguationData":[OSD([sQuery(id+"F38.wireOp",EDGE,"E105")])],"isStart":false})});
            var sketch = newSketch(context, id + "F40", { "sketchPlane" : qUnion([Q0])});
            skArc(sketch, "E106.0", {"start": v(-7.08, -14.35) * mm, "mid": v(0, 16) * mm, "end": v(7.08, -14.35) * mm});
            skCircle(sketch, "E107", {"center": v(0, 0) * mm, "radius": 16 * mm});
            skSolve(sketch);
        }
        {
            var Q0;
            Q0 = qSketchRegion(id + "F40", true);
            extrude(context, id + "F41", {"entities" : qUnion([Q0]), "operationType" : NewBodyOperationType.ADD, "oppositeDirection" : true, "depth" : 18.26 * mm});
        }
        {
            var Q0;
            {var subQ0=sQuery(id+"F11.wireOp",EDGE,"E45.0");var subQ2=sQuery(id+"F11.wireOp",EDGE,"E44.0");var subQ3=sQuery(id+"F11.wireOp",EDGE,"E43.0");var subQ4=sQuery(id+"F11.wireOp",EDGE,"E56");var subQ5=sQuery(id+"F11.wireOp",EDGE,"E42.0");var subQ6=sQuery(id+"F11.wireOp",EDGE,"E57");var subQ7=sQuery(id+"F11.wireOp",EDGE,"E55.0");var subQ8=sQuery(id+"F11.wireOp",EDGE,"E54.0");var subQ9=sQuery(id+"F11.wireOp",EDGE,"E53.0");var subQ10=sQuery(id+"F11.wireOp",EDGE,"E52.0");var subQ11=sQuery(id+"F11.wireOp",EDGE,"E50.0");var subQ12=sQuery(id+"F11.wireOp",EDGE,"E49.0");var subQ13=sQuery(id+"F11.wireOp",EDGE,"E48.0");var subQ14=sQuery(id+"F11.wireOp",EDGE,"E47.0");var subQ15=sQuery(id+"F11.wireOp",EDGE,"E46.0");var subQ16=makeQuery(id+"F12.opExtrude","CAP_FACE",FACE,{"disambiguationData":[OSD([subQ5,subQ3,subQ2,subQ0,subQ15,subQ14,subQ13,subQ12,subQ11,subQ10,subQ9,subQ8,subQ7,subQ4,subQ6,sQuery(id+"F11.wireOp",EDGE,"E60")])],"isStart":true});Q0=makeQuery(id+"F29.boolean.opBoolean","MERGE",FACE,{"derivedFrom":[makeQuery(id+"F17.opBoolean","SPLIT",FACE,{"disambiguationData":[TD([makeQuery(id+"F7.opExtrude","SWEPT_FACE",FACE,{"disambiguationData":[OSD([sQuery(id+"F6.wireOp",EDGE,"E33")])]})])],"derivedFrom":subQ16}),makeQuery(id+"F29.opExtrude","CAP_FACE",FACE,{"disambiguationData":[OSD([sQuery(id+"F28.wireOp",EDGE,"E88.0"),sQuery(id+"F28.wireOp",EDGE,"E89"),sQuery(id+"F28.wireOp",EDGE,"E90"),sQuery(id+"F28.wireOp",EDGE,"E91"),sQuery(id+"F28.wireOp",EDGE,"E92")])],"isStart":true})]});}
            var sketch = newSketch(context, id + "F42", { "sketchPlane" : qUnion([Q0])});
            skLineSegment(sketch, "E108.bottom", {"start": v(-23.69, 20.83) * mm, "end": v(24.1, 20.83) * mm});
            skLineSegment(sketch, "E108.top", {"start": v(-23.69, -21.5) * mm, "end": v(24.1, -21.5) * mm});
            skLineSegment(sketch, "E108.left", {"start": v(-23.69, 20.83) * mm, "end": v(-23.69, -21.5) * mm});
            skLineSegment(sketch, "E108.right", {"start": v(24.1, 20.83) * mm, "end": v(24.1, -21.5) * mm});
            skSolve(sketch);
        }
        {
            var Q0;
            Q0 = qSketchRegion(id + "F42", true);
            extrude(context, id + "F43", {"entities" : qUnion([Q0]), "operationType" : NewBodyOperationType.REMOVE, "endBound" : BoundingType.THROUGH_ALL, "depth" : 25 * mm});
        }
        {
            var Q0;
            Q0=sQuery(id+"F36.wireOp",EDGE,"E103");
            var Q1;
            Q1=qCreatedBy(id+"F37.planeOp",FACE);
            cPlane(context, id + "F44", {"entities" : qUnion([Q0, Q1]), "cplaneType" : CPlaneType.LINE_ANGLE, "offset" : 150 * mm, "angle" : 90 * degree, "width" : 150 * mm, "height" : 150 * mm});
        }
        {
            var Q0;
            Q0=qCreatedBy(id+"F44.planeOp",FACE);
            var sketch = newSketch(context, id + "F45", { "sketchPlane" : qUnion([Q0])});
            skLineSegment(sketch, "E109.0", {"start": v(16, -1.5) * mm, "end": v(-16, -1.5) * mm});
            skLineSegment(sketch, "E110.0", {"start": v(16, -19.77) * mm, "end": v(-16, -19.77) * mm});
            skLineSegment(sketch, "E111", {"start": v(0, -19.77) * mm, "end": v(0, 19.85) * mm});
            skLineSegment(sketch, "E112", {"start": v(8.25, -19.77) * mm, "end": v(6.27, 12.23) * mm});
            skLineSegment(sketch, "E113", {"start": v(6.27, 12.23) * mm, "end": v(0, 12.23) * mm});
            skSolve(sketch);
        }
        {
            var Q0;
            {var subQ0=sQuery(id+"F45.wireOp",EDGE,"E111");var subQ1=sQuery(id+"F45.wireOp",EDGE,"E109.0");var subQ2=makeQuery(id+"F45.imprint","INTERSECT",VERTEX,{"derivedFrom":[subQ1,subQ0]});Q0=makeQuery(id+"F45.imprint","IMPRINT",FACE,{"disambiguationData":[TD([[makeQuery(id+"F45.imprint","IMPRINT",EDGE,{"disambiguationData":[TD([[subQ2,1.0]])],"derivedFrom":subQ1}),1.0]])]});}
            var Q1;
            {var subQ5=sQuery(id+"F45.wireOp",EDGE,"E113");Q1=makeQuery(id+"F45.imprint","IMPRINT",FACE,{"disambiguationData":[TD([[makeQuery(id+"F45.imprint","IMPRINT",EDGE,{"derivedFrom":subQ5}),1.0]])]});}
            var Q2;
            Q2=sQuery(id+"F45.wireOp",EDGE,"E111");
            revolve(context, id + "F46", {"operationType" : NewBodyOperationType.REMOVE, "entities" : qUnion([Q0, Q1]), "axis" : qUnion([Q2]), "revolveType" : RevolveType.FULL, "oppositeDirection" : true});
        }
        {
            var Q0;
            Q0=makeQuery(id+"F7.opExtrude","CAP_FACE",FACE,{"disambiguationData":[OSD([sQuery(id+"F6.wireOp",EDGE,"E31"),sQuery(id+"F6.wireOp",EDGE,"E33"),sQuery(id+"F6.wireOp",EDGE,"E34"),sQuery(id+"F6.wireOp",EDGE,"E35"),sQuery(id+"F6.wireOp",EDGE,"E36")])],"isStart":true});
            var sketch = newSketch(context, id + "F47", { "sketchPlane" : qUnion([Q0])});
            skLineSegment(sketch, "E114.0", {"start": v(96.03, 20.7) * mm, "end": v(112, 21.54) * mm, "construction": true});
            skLineSegment(sketch, "E115.0", {"start": v(97.73, -11.26) * mm, "end": v(113.7, -10.41) * mm, "construction": true});
            skCircle(sketch, "E116.0", {"center": v(112.86, 5.56) * mm, "radius": 5 * mm, "construction": true});
            skLineSegment(sketch, "E117", {"start": v(88.7, 4.28) * mm, "end": v(141.54, 7.09) * mm, "construction": true});
            skSolve(sketch);
        }
        {
            var Q0;
            Q0=sQuery(id+"F47.wireOp",EDGE,"E117");
            var Q1;
            Q1=makeQuery(id+"F47.imprint","IMPRINT",FACE,{"disambiguationData":[TD([[makeQuery(id+"F47.imprint","IMPRINT",EDGE,{"derivedFrom":makeQuery(id+"F7.opExtrude","CAP_EDGE",EDGE,{"disambiguationData":[OSD([sQuery(id+"F6.wireOp",EDGE,"E31")])],"isStart":true})}),1.0]])]});
            cPlane(context, id + "F48", {"entities" : qUnion([Q0, Q1]), "cplaneType" : CPlaneType.LINE_ANGLE, "offset" : 150 * mm, "angle" : 90 * degree, "width" : 150 * mm, "height" : 150 * mm});
        }
        {
            var Q0;
            Q0=qCreatedBy(id+"F48.planeOp",FACE);
            var sketch = newSketch(context, id + "F49", { "sketchPlane" : qUnion([Q0])});
            skLineSegment(sketch, "E118.0", {"start": v(-117.61, 9.67) * mm, "end": v(-107.66, 8.7) * mm});
            skLineSegment(sketch, "E119.0", {"start": v(-119.17, -6.26) * mm, "end": v(-109.21, -7.23) * mm});
            skLineSegment(sketch, "E120", {"start": v(-114.19, -6.74) * mm, "end": v(-111.77, 18) * mm});
            skLineSegment(sketch, "E121", {"start": v(-114.19, -6.74) * mm, "end": v(-121.26, -6.05) * mm});
            skLineSegment(sketch, "E122", {"start": v(-121.26, -6.05) * mm, "end": v(-118.33, 13.76) * mm});
            skLineSegment(sketch, "E123", {"start": v(-118.33, 13.76) * mm, "end": v(-112.25, 13.16) * mm});
            skSolve(sketch);
        }
        {
            var Q0;
            {var subQ4=sQuery(id+"F49.wireOp",EDGE,"E122");Q0=makeQuery(id+"F49.imprint","IMPRINT",FACE,{"disambiguationData":[TD([[makeQuery(id+"F49.imprint","IMPRINT",EDGE,{"derivedFrom":subQ4}),-1.0]])]});}
            var Q1;
            Q1=sQuery(id+"F49.wireOp",EDGE,"E120");
            revolve(context, id + "F50", {"operationType" : NewBodyOperationType.REMOVE, "entities" : qUnion([Q0]), "axis" : qUnion([Q1]), "revolveType" : RevolveType.FULL, "oppositeDirection" : true});
        }
        {
            var Q0;
            Q0=makeQuery(id+"F0.imprint","IMPRINT",FACE,{"disambiguationData":[TD([[makeQuery(id+"F0.imprint","IMPRINT",EDGE,{"derivedFrom":sQuery(id+"F0.wireOp",EDGE,"E6")}),-1.0]])]});
            var Q1;
            Q1=makeQuery(id+"F0.imprint","IMPRINT",FACE,{"disambiguationData":[TD([[makeQuery(id+"F0.imprint","IMPRINT",EDGE,{"derivedFrom":sQuery(id+"F0.wireOp",EDGE,"E2")}),-1.0]])]});
            extrude(context, id + "F51", {"entities" : qUnion([Q0, Q1]), "operationType" : NewBodyOperationType.REMOVE, "oppositeDirection" : true, "depth" : 6 * mm});
        }
        {
            var Q0;
            Q0=qCreatedBy(makeId("Right.planeOp"),FACE);
            var sketch = newSketch(context, id + "F52", { "sketchPlane" : qUnion([Q0])});
            skLineSegment(sketch, "E124", {"start": v(-23.5, -0.4) * mm, "end": v(33.5, -15.6) * mm});
            skLineSegment(sketch, "E125", {"start": v(33.5, -0.4) * mm, "end": v(-23.5, -15.6) * mm});
            skCircle(sketch, "E126", {"center": v(5, -8) * mm, "radius": 29.5 * mm});
            skCircle(sketch, "E127", {"center": v(5, -8) * mm, "radius": 39.77 * mm});
            skPoint(sketch, "E128.orphan", {"position": v(35, -16) * mm});
            skPoint(sketch, "E129.orphan", {"position": v(-25, 0) * mm});
            skSolve(sketch);
        }
        {
            var Q0;
            Q0=makeQuery(id+"F52.imprint","IMPRINT",FACE,{"disambiguationData":[TD([[makeQuery(id+"F52.imprint","IMPRINT",EDGE,{"derivedFrom":sQuery(id+"F52.wireOp",EDGE,"E127")}),1.0]])]});
            extrude(context, id + "F53", {"entities" : qUnion([Q0]), "operationType" : NewBodyOperationType.REMOVE, "endBound" : BoundingType.THROUGH_ALL, "oppositeDirection" : true, "depth" : 25 * mm, "hasSecondDirection" : true, "secondDirectionBound" : BoundingType.THROUGH_ALL, "secondDirectionOppositeDirection" : false, "secondDirectionDepth" : 25 * mm});
        }
        {
            var Q0;
            Q0=makeQuery(id+"F10.boolean.opBoolean","MERGE",EDGE,{"derivedFrom":[makeQuery(id+"F7.opExtrude","CAP_EDGE",EDGE,{"disambiguationData":[OSD([sQuery(id+"F6.wireOp",EDGE,"E35")])],"isStart":true}),makeQuery(id+"F10.opExtrude","CAP_EDGE",EDGE,{"disambiguationData":[OSD([sQuery(id+"F9.wireOp",EDGE,"E37.0")])],"isStart":true})]});
            var Q1;
            Q1=makeQuery(id+"F31.boolean.opBoolean","MERGE",EDGE,{"derivedFrom":[makeQuery(id+"F17.opBoolean","INTERSECT",EDGE,{"derivedFrom":[makeQuery(id+"F10.opExtrude","CAP_FACE",FACE,{"disambiguationData":[OSD([sQuery(id+"F9.wireOp",EDGE,"E37.0"),sQuery(id+"F9.wireOp",EDGE,"E39"),sQuery(id+"F9.wireOp",EDGE,"E40"),sQuery(id+"F9.wireOp",EDGE,"E41")])],"isStart":true}),makeQuery(id+"F12.opExtrude","CAP_FACE",FACE,{"disambiguationData":[OSD([sQuery(id+"F11.wireOp",EDGE,"E42.0"),sQuery(id+"F11.wireOp",EDGE,"E43.0"),sQuery(id+"F11.wireOp",EDGE,"E44.0"),sQuery(id+"F11.wireOp",EDGE,"E45.0"),sQuery(id+"F11.wireOp",EDGE,"E46.0"),sQuery(id+"F11.wireOp",EDGE,"E47.0"),sQuery(id+"F11.wireOp",EDGE,"E48.0"),sQuery(id+"F11.wireOp",EDGE,"E49.0"),sQuery(id+"F11.wireOp",EDGE,"E50.0"),sQuery(id+"F11.wireOp",EDGE,"E52.0"),sQuery(id+"F11.wireOp",EDGE,"E53.0"),sQuery(id+"F11.wireOp",EDGE,"E54.0"),sQuery(id+"F11.wireOp",EDGE,"E55.0"),sQuery(id+"F11.wireOp",EDGE,"E56"),sQuery(id+"F11.wireOp",EDGE,"E57"),sQuery(id+"F11.wireOp",EDGE,"E60")])],"isStart":true})]}),makeQuery(id+"F29.boolean.opBoolean","COPY",EDGE,{"derivedFrom":makeQuery(id+"F29.opExtrude","CAP_EDGE",EDGE,{"disambiguationData":[OSD([sQuery(id+"F28.wireOp",EDGE,"E88.0"),sQuery(id+"F28.wireOp",EDGE,"E89")])],"isStart":true})}),makeQuery(id+"F31.opExtrude","CAP_EDGE",EDGE,{"disambiguationData":[OSD([sQuery(id+"F30.wireOp",EDGE,"E93.0"),sQuery(id+"F30.wireOp",EDGE,"E94")])],"isStart":true})]});
            var Q2;
            Q2=makeQuery(id+"F10.boolean.opBoolean","INTERSECT",EDGE,{"derivedFrom":[makeQuery(id+"F7.opExtrude","CAP_FACE",FACE,{"disambiguationData":[OSD([sQuery(id+"F6.wireOp",EDGE,"E31"),sQuery(id+"F6.wireOp",EDGE,"E33"),sQuery(id+"F6.wireOp",EDGE,"E34"),sQuery(id+"F6.wireOp",EDGE,"E35"),sQuery(id+"F6.wireOp",EDGE,"E36")])],"isStart":false}),makeQuery(id+"F10.opExtrude","CAP_FACE",FACE,{"disambiguationData":[OSD([sQuery(id+"F9.wireOp",EDGE,"E37.0"),sQuery(id+"F9.wireOp",EDGE,"E39"),sQuery(id+"F9.wireOp",EDGE,"E40"),sQuery(id+"F9.wireOp",EDGE,"E41")])],"isStart":false})]});
            var Q3;
            Q3=makeQuery(id+"F17.opBoolean","MERGE",EDGE,{"derivedFrom":[makeQuery(id+"F14.boolean.opBoolean","INTERSECT",EDGE,{"derivedFrom":[makeQuery(id+"F12.opExtrude","CAP_FACE",FACE,{"disambiguationData":[OSD([sQuery(id+"F11.wireOp",EDGE,"E42.0"),sQuery(id+"F11.wireOp",EDGE,"E43.0"),sQuery(id+"F11.wireOp",EDGE,"E44.0"),sQuery(id+"F11.wireOp",EDGE,"E45.0"),sQuery(id+"F11.wireOp",EDGE,"E46.0"),sQuery(id+"F11.wireOp",EDGE,"E47.0"),sQuery(id+"F11.wireOp",EDGE,"E48.0"),sQuery(id+"F11.wireOp",EDGE,"E49.0"),sQuery(id+"F11.wireOp",EDGE,"E50.0"),sQuery(id+"F11.wireOp",EDGE,"E52.0"),sQuery(id+"F11.wireOp",EDGE,"E53.0"),sQuery(id+"F11.wireOp",EDGE,"E54.0"),sQuery(id+"F11.wireOp",EDGE,"E55.0"),sQuery(id+"F11.wireOp",EDGE,"E56"),sQuery(id+"F11.wireOp",EDGE,"E57"),sQuery(id+"F11.wireOp",EDGE,"E60")])],"isStart":false}),makeQuery(id+"F14.opExtrude","CAP_FACE",FACE,{"disambiguationData":[OSD([sQuery(id+"F13.wireOp",EDGE,"E61.bottom"),sQuery(id+"F13.wireOp",EDGE,"E61.top"),sQuery(id+"F13.wireOp",EDGE,"E61.left"),sQuery(id+"F13.wireOp",EDGE,"E61.right")])],"isStart":true})]}),makeQuery(id+"F16.boolean.opBoolean","INTERSECT",EDGE,{"derivedFrom":[makeQuery(id+"F10.opExtrude","CAP_FACE",FACE,{"disambiguationData":[OSD([sQuery(id+"F9.wireOp",EDGE,"E37.0"),sQuery(id+"F9.wireOp",EDGE,"E39"),sQuery(id+"F9.wireOp",EDGE,"E40"),sQuery(id+"F9.wireOp",EDGE,"E41")])],"isStart":false}),makeQuery(id+"F16.opExtrude","CAP_FACE",FACE,{"disambiguationData":[OSD([sQuery(id+"F15.wireOp",EDGE,"E62.bottom"),sQuery(id+"F15.wireOp",EDGE,"E62.top"),sQuery(id+"F15.wireOp",EDGE,"E62.left"),sQuery(id+"F15.wireOp",EDGE,"E62.right")])],"isStart":true})]})]});
            fillet(context, id + "F54", {"entities" : qUnion([Q0, Q1, Q2, Q3]), "radius" : 30 * mm, "tangentPropagation" : true, "allowEdgeOverflow" : false});
        }
        {
            var Q0;
            Q0=makeQuery(id+"F7.opExtrude","CAP_EDGE",EDGE,{"disambiguationData":[OSD([sQuery(id+"F6.wireOp",EDGE,"E33")])],"isStart":true});
            var Q1;
            Q1=makeQuery(id+"F12.opExtrude","CAP_EDGE",EDGE,{"disambiguationData":[OSD([sQuery(id+"F11.wireOp",EDGE,"E44.0")])],"isStart":true});
            var Q2;
            {var subQ0=sQuery(id+"F11.wireOp",EDGE,"E45.0");var subQ2=sQuery(id+"F11.wireOp",EDGE,"E44.0");var subQ3=sQuery(id+"F11.wireOp",EDGE,"E43.0");var subQ4=sQuery(id+"F11.wireOp",EDGE,"E56");var subQ5=sQuery(id+"F11.wireOp",EDGE,"E42.0");var subQ6=sQuery(id+"F11.wireOp",EDGE,"E57");var subQ7=sQuery(id+"F11.wireOp",EDGE,"E55.0");var subQ8=sQuery(id+"F11.wireOp",EDGE,"E54.0");var subQ9=sQuery(id+"F11.wireOp",EDGE,"E53.0");var subQ10=sQuery(id+"F11.wireOp",EDGE,"E52.0");var subQ11=sQuery(id+"F11.wireOp",EDGE,"E50.0");var subQ12=sQuery(id+"F11.wireOp",EDGE,"E49.0");var subQ13=sQuery(id+"F11.wireOp",EDGE,"E48.0");var subQ14=sQuery(id+"F11.wireOp",EDGE,"E47.0");var subQ15=sQuery(id+"F11.wireOp",EDGE,"E46.0");var subQ16=makeQuery(id+"F12.opExtrude","CAP_FACE",FACE,{"disambiguationData":[OSD([subQ5,subQ3,subQ2,subQ0,subQ15,subQ14,subQ13,subQ12,subQ11,subQ10,subQ9,subQ8,subQ7,subQ4,subQ6,sQuery(id+"F11.wireOp",EDGE,"E60")])],"isStart":true});Q2=makeQuery(id+"F53.boolean.opBoolean","INTERSECT",EDGE,{"disambiguationData":[OD(0.0)],"derivedFrom":[makeQuery(id+"F43.boolean.opBoolean","MERGE",FACE,{"derivedFrom":[makeQuery(id+"F29.boolean.opBoolean","MERGE",FACE,{"derivedFrom":[makeQuery(id+"F17.opBoolean","SPLIT",FACE,{"disambiguationData":[TD([makeQuery(id+"F7.opExtrude","SWEPT_FACE",FACE,{"disambiguationData":[OSD([sQuery(id+"F6.wireOp",EDGE,"E33")])]})])],"derivedFrom":subQ16}),makeQuery(id+"F29.opExtrude","CAP_FACE",FACE,{"disambiguationData":[OSD([sQuery(id+"F28.wireOp",EDGE,"E88.0"),sQuery(id+"F28.wireOp",EDGE,"E89"),sQuery(id+"F28.wireOp",EDGE,"E90"),sQuery(id+"F28.wireOp",EDGE,"E91"),sQuery(id+"F28.wireOp",EDGE,"E92")])],"isStart":true})]}),makeQuery(id+"F43.opExtrude","CAP_FACE",FACE,{"disambiguationData":[OSD([sQuery(id+"F42.wireOp",EDGE,"E108.bottom"),sQuery(id+"F42.wireOp",EDGE,"E108.top"),sQuery(id+"F42.wireOp",EDGE,"E108.left"),sQuery(id+"F42.wireOp",EDGE,"E108.right")])],"isStart":true})]}),makeQuery(id+"F53.opExtrude","SWEPT_FACE",FACE,{"disambiguationData":[OSD([sQuery(id+"F52.wireOp",EDGE,"E126")])]})]});}
            var Q3;
            {var subQ0=sQuery(id+"F11.wireOp",EDGE,"E45.0");var subQ2=sQuery(id+"F11.wireOp",EDGE,"E44.0");var subQ3=sQuery(id+"F11.wireOp",EDGE,"E43.0");var subQ4=sQuery(id+"F11.wireOp",EDGE,"E56");var subQ5=sQuery(id+"F11.wireOp",EDGE,"E42.0");var subQ6=sQuery(id+"F11.wireOp",EDGE,"E57");var subQ7=sQuery(id+"F11.wireOp",EDGE,"E55.0");var subQ8=sQuery(id+"F11.wireOp",EDGE,"E54.0");var subQ9=sQuery(id+"F11.wireOp",EDGE,"E53.0");var subQ10=sQuery(id+"F11.wireOp",EDGE,"E52.0");var subQ11=sQuery(id+"F11.wireOp",EDGE,"E50.0");var subQ12=sQuery(id+"F11.wireOp",EDGE,"E49.0");var subQ13=sQuery(id+"F11.wireOp",EDGE,"E48.0");var subQ14=sQuery(id+"F11.wireOp",EDGE,"E47.0");var subQ15=sQuery(id+"F11.wireOp",EDGE,"E46.0");var subQ16=makeQuery(id+"F12.opExtrude","CAP_FACE",FACE,{"disambiguationData":[OSD([subQ5,subQ3,subQ2,subQ0,subQ15,subQ14,subQ13,subQ12,subQ11,subQ10,subQ9,subQ8,subQ7,subQ4,subQ6,sQuery(id+"F11.wireOp",EDGE,"E60")])],"isStart":true});Q3=makeQuery(id+"F53.boolean.opBoolean","INTERSECT",EDGE,{"disambiguationData":[OD(1.0)],"derivedFrom":[makeQuery(id+"F43.boolean.opBoolean","MERGE",FACE,{"derivedFrom":[makeQuery(id+"F29.boolean.opBoolean","MERGE",FACE,{"derivedFrom":[makeQuery(id+"F17.opBoolean","SPLIT",FACE,{"disambiguationData":[TD([makeQuery(id+"F7.opExtrude","SWEPT_FACE",FACE,{"disambiguationData":[OSD([sQuery(id+"F6.wireOp",EDGE,"E33")])]})])],"derivedFrom":subQ16}),makeQuery(id+"F29.opExtrude","CAP_FACE",FACE,{"disambiguationData":[OSD([sQuery(id+"F28.wireOp",EDGE,"E88.0"),sQuery(id+"F28.wireOp",EDGE,"E89"),sQuery(id+"F28.wireOp",EDGE,"E90"),sQuery(id+"F28.wireOp",EDGE,"E91"),sQuery(id+"F28.wireOp",EDGE,"E92")])],"isStart":true})]}),makeQuery(id+"F43.opExtrude","CAP_FACE",FACE,{"disambiguationData":[OSD([sQuery(id+"F42.wireOp",EDGE,"E108.bottom"),sQuery(id+"F42.wireOp",EDGE,"E108.top"),sQuery(id+"F42.wireOp",EDGE,"E108.left"),sQuery(id+"F42.wireOp",EDGE,"E108.right")])],"isStart":true})]}),makeQuery(id+"F53.opExtrude","SWEPT_FACE",FACE,{"disambiguationData":[OSD([sQuery(id+"F52.wireOp",EDGE,"E126")])]})]});}
            var Q4;
            Q4=makeQuery(id+"F7.opExtrude","CAP_EDGE",EDGE,{"disambiguationData":[OSD([sQuery(id+"F6.wireOp",EDGE,"E34")])],"isStart":false});
            var Q5;
            Q5=makeQuery(id+"F12.opExtrude","CAP_EDGE",EDGE,{"disambiguationData":[OSD([sQuery(id+"F11.wireOp",EDGE,"E48.0")])],"isStart":false});
            var Q6;
            Q6=makeQuery(id+"F53.boolean.opBoolean","INTERSECT",EDGE,{"disambiguationData":[OD(1.0)],"derivedFrom":[makeQuery(id+"F25.boolean.opBoolean","MERGE",FACE,{"derivedFrom":[makeQuery(id+"F17.opBoolean","MERGE",FACE,{"derivedFrom":[makeQuery(id+"F12.opExtrude","CAP_FACE",FACE,{"disambiguationData":[OSD([sQuery(id+"F11.wireOp",EDGE,"E42.0"),sQuery(id+"F11.wireOp",EDGE,"E43.0"),sQuery(id+"F11.wireOp",EDGE,"E44.0"),sQuery(id+"F11.wireOp",EDGE,"E45.0"),sQuery(id+"F11.wireOp",EDGE,"E46.0"),sQuery(id+"F11.wireOp",EDGE,"E47.0"),sQuery(id+"F11.wireOp",EDGE,"E48.0"),sQuery(id+"F11.wireOp",EDGE,"E49.0"),sQuery(id+"F11.wireOp",EDGE,"E50.0"),sQuery(id+"F11.wireOp",EDGE,"E52.0"),sQuery(id+"F11.wireOp",EDGE,"E53.0"),sQuery(id+"F11.wireOp",EDGE,"E54.0"),sQuery(id+"F11.wireOp",EDGE,"E55.0"),sQuery(id+"F11.wireOp",EDGE,"E56"),sQuery(id+"F11.wireOp",EDGE,"E57"),sQuery(id+"F11.wireOp",EDGE,"E60")])],"isStart":false}),makeQuery(id+"F16.boolean.opBoolean","COPY",FACE,{"derivedFrom":makeQuery(id+"F16.opExtrude","CAP_FACE",FACE,{"disambiguationData":[OSD([sQuery(id+"F15.wireOp",EDGE,"E62.bottom"),sQuery(id+"F15.wireOp",EDGE,"E62.top"),sQuery(id+"F15.wireOp",EDGE,"E62.left"),sQuery(id+"F15.wireOp",EDGE,"E62.right")])],"isStart":true})})]}),makeQuery(id+"F25.opExtrude","SWEPT_FACE",FACE,{"disambiguationData":[OSD([sQuery(id+"F24.wireOp",EDGE,"E78.0.2"),sQuery(id+"F24.wireOp",EDGE,"E79")])]})]}),makeQuery(id+"F53.opExtrude","SWEPT_FACE",FACE,{"disambiguationData":[OSD([sQuery(id+"F52.wireOp",EDGE,"E126")])]})]});
            var Q7;
            Q7=makeQuery(id+"F53.boolean.opBoolean","INTERSECT",EDGE,{"disambiguationData":[OD(0.0)],"derivedFrom":[makeQuery(id+"F25.boolean.opBoolean","MERGE",FACE,{"derivedFrom":[makeQuery(id+"F17.opBoolean","MERGE",FACE,{"derivedFrom":[makeQuery(id+"F12.opExtrude","CAP_FACE",FACE,{"disambiguationData":[OSD([sQuery(id+"F11.wireOp",EDGE,"E42.0"),sQuery(id+"F11.wireOp",EDGE,"E43.0"),sQuery(id+"F11.wireOp",EDGE,"E44.0"),sQuery(id+"F11.wireOp",EDGE,"E45.0"),sQuery(id+"F11.wireOp",EDGE,"E46.0"),sQuery(id+"F11.wireOp",EDGE,"E47.0"),sQuery(id+"F11.wireOp",EDGE,"E48.0"),sQuery(id+"F11.wireOp",EDGE,"E49.0"),sQuery(id+"F11.wireOp",EDGE,"E50.0"),sQuery(id+"F11.wireOp",EDGE,"E52.0"),sQuery(id+"F11.wireOp",EDGE,"E53.0"),sQuery(id+"F11.wireOp",EDGE,"E54.0"),sQuery(id+"F11.wireOp",EDGE,"E55.0"),sQuery(id+"F11.wireOp",EDGE,"E56"),sQuery(id+"F11.wireOp",EDGE,"E57"),sQuery(id+"F11.wireOp",EDGE,"E60")])],"isStart":false}),makeQuery(id+"F16.boolean.opBoolean","COPY",FACE,{"derivedFrom":makeQuery(id+"F16.opExtrude","CAP_FACE",FACE,{"disambiguationData":[OSD([sQuery(id+"F15.wireOp",EDGE,"E62.bottom"),sQuery(id+"F15.wireOp",EDGE,"E62.top"),sQuery(id+"F15.wireOp",EDGE,"E62.left"),sQuery(id+"F15.wireOp",EDGE,"E62.right")])],"isStart":true})})]}),makeQuery(id+"F25.opExtrude","SWEPT_FACE",FACE,{"disambiguationData":[OSD([sQuery(id+"F24.wireOp",EDGE,"E78.0.2"),sQuery(id+"F24.wireOp",EDGE,"E79")])]})]}),makeQuery(id+"F53.opExtrude","SWEPT_FACE",FACE,{"disambiguationData":[OSD([sQuery(id+"F52.wireOp",EDGE,"E126")])]})]});
            fillet(context, id + "F55", {"entities" : qUnion([Q0, Q1, Q2, Q3, Q4, Q5, Q6, Q7]), "radius" : 2 * mm, "tangentPropagation" : true, "allowEdgeOverflow" : false});
        }
        {
            var Q0;
            Q0=makeQuery(id+"F41.opExtrude","CAP_EDGE",EDGE,{"disambiguationData":[OSD([sQuery(id+"F40.wireOp",EDGE,"E107")])],"isStart":false});
            fillet(context, id + "F56", {"entities" : qUnion([Q0]), "radius" : 2 * mm, "tangentPropagation" : true, "allowEdgeOverflow" : false});
        }
        {
            var Q0;
            Q0=makeQuery(id+"F41.boolean.opBoolean","INTERSECT",EDGE,{"derivedFrom":[makeQuery(id+"F25.boolean.opBoolean","MERGE",FACE,{"derivedFrom":[makeQuery(id+"F17.opBoolean","MERGE",FACE,{"derivedFrom":[makeQuery(id+"F12.opExtrude","CAP_FACE",FACE,{"disambiguationData":[OSD([sQuery(id+"F11.wireOp",EDGE,"E42.0"),sQuery(id+"F11.wireOp",EDGE,"E43.0"),sQuery(id+"F11.wireOp",EDGE,"E44.0"),sQuery(id+"F11.wireOp",EDGE,"E45.0"),sQuery(id+"F11.wireOp",EDGE,"E46.0"),sQuery(id+"F11.wireOp",EDGE,"E47.0"),sQuery(id+"F11.wireOp",EDGE,"E48.0"),sQuery(id+"F11.wireOp",EDGE,"E49.0"),sQuery(id+"F11.wireOp",EDGE,"E50.0"),sQuery(id+"F11.wireOp",EDGE,"E52.0"),sQuery(id+"F11.wireOp",EDGE,"E53.0"),sQuery(id+"F11.wireOp",EDGE,"E54.0"),sQuery(id+"F11.wireOp",EDGE,"E55.0"),sQuery(id+"F11.wireOp",EDGE,"E56"),sQuery(id+"F11.wireOp",EDGE,"E57"),sQuery(id+"F11.wireOp",EDGE,"E60")])],"isStart":false}),makeQuery(id+"F16.boolean.opBoolean","COPY",FACE,{"derivedFrom":makeQuery(id+"F16.opExtrude","CAP_FACE",FACE,{"disambiguationData":[OSD([sQuery(id+"F15.wireOp",EDGE,"E62.bottom"),sQuery(id+"F15.wireOp",EDGE,"E62.top"),sQuery(id+"F15.wireOp",EDGE,"E62.left"),sQuery(id+"F15.wireOp",EDGE,"E62.right")])],"isStart":true})})]}),makeQuery(id+"F25.opExtrude","SWEPT_FACE",FACE,{"disambiguationData":[OSD([sQuery(id+"F24.wireOp",EDGE,"E78.0.2"),sQuery(id+"F24.wireOp",EDGE,"E79")])]})]}),makeQuery(id+"F41.opExtrude","SWEPT_FACE",FACE,{"disambiguationData":[OSD([sQuery(id+"F40.wireOp",EDGE,"E107")])]})]});
            var Q1;
            Q1=makeQuery(id+"F39.boolean.opBoolean","COPY",EDGE,{"derivedFrom":makeQuery(id+"F39.opExtrude","CAP_EDGE",EDGE,{"disambiguationData":[OSD([sQuery(id+"F38.wireOp",EDGE,"E105")])],"isStart":false})});
            var Q2;
            {var subQ0=sQuery(id+"F11.wireOp",EDGE,"E45.0");var subQ2=sQuery(id+"F11.wireOp",EDGE,"E44.0");var subQ3=sQuery(id+"F11.wireOp",EDGE,"E43.0");var subQ4=sQuery(id+"F11.wireOp",EDGE,"E56");var subQ5=sQuery(id+"F11.wireOp",EDGE,"E42.0");var subQ6=sQuery(id+"F11.wireOp",EDGE,"E57");var subQ7=sQuery(id+"F11.wireOp",EDGE,"E55.0");var subQ8=sQuery(id+"F11.wireOp",EDGE,"E54.0");var subQ9=sQuery(id+"F11.wireOp",EDGE,"E53.0");var subQ10=sQuery(id+"F11.wireOp",EDGE,"E52.0");var subQ11=sQuery(id+"F11.wireOp",EDGE,"E50.0");var subQ12=sQuery(id+"F11.wireOp",EDGE,"E49.0");var subQ13=sQuery(id+"F11.wireOp",EDGE,"E48.0");var subQ14=sQuery(id+"F11.wireOp",EDGE,"E47.0");var subQ15=sQuery(id+"F11.wireOp",EDGE,"E46.0");var subQ16=makeQuery(id+"F12.opExtrude","CAP_FACE",FACE,{"disambiguationData":[OSD([subQ5,subQ3,subQ2,subQ0,subQ15,subQ14,subQ13,subQ12,subQ11,subQ10,subQ9,subQ8,subQ7,subQ4,subQ6,sQuery(id+"F11.wireOp",EDGE,"E60")])],"isStart":true});Q2=makeQuery(id+"F39.boolean.opBoolean","INTERSECT",EDGE,{"derivedFrom":[makeQuery(id+"F29.boolean.opBoolean","MERGE",FACE,{"derivedFrom":[makeQuery(id+"F17.opBoolean","SPLIT",FACE,{"disambiguationData":[TD([makeQuery(id+"F7.opExtrude","SWEPT_FACE",FACE,{"disambiguationData":[OSD([sQuery(id+"F6.wireOp",EDGE,"E33")])]})])],"derivedFrom":subQ16}),makeQuery(id+"F29.opExtrude","CAP_FACE",FACE,{"disambiguationData":[OSD([sQuery(id+"F28.wireOp",EDGE,"E88.0"),sQuery(id+"F28.wireOp",EDGE,"E89"),sQuery(id+"F28.wireOp",EDGE,"E90"),sQuery(id+"F28.wireOp",EDGE,"E91"),sQuery(id+"F28.wireOp",EDGE,"E92")])],"isStart":true})]}),makeQuery(id+"F39.opExtrude","SWEPT_FACE",FACE,{"disambiguationData":[OSD([sQuery(id+"F38.wireOp",EDGE,"E105")])]})]});}
            fillet(context, id + "F57", {"entities" : qUnion([Q0, Q1, Q2]), "radius" : 0.8 * mm, "tangentPropagation" : true, "allowEdgeOverflow" : false});
        }
    });
